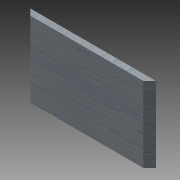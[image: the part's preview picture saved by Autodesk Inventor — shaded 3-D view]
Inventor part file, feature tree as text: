
AUTODESK INVENTOR PART (.ipt)
format: ipt  version: 2011 SP1 (Build 150282100, 282)  size: 86,528 bytes
history: native  units: in
note: dims shown in document units (in); Inventor stores cm internally (conversion verified against a paired STEP export)
features: extrude x1, chamfer x1, sketch x1
ambient origin geometry x8: Origin, YZ Plane, XZ Plane, XY Plane, X Axis, Y Axis, Z Axis, Center Point
bodies: Solid1 (feature_tree)
feature tree (3):
  extrude  "Extrusion1"  Depth=1.5in
  chamfer  "Chamfer1"  Distance=0.125in
  sketch  "Sketch1"  dims[d0=2.5in d1=1.5in d2=0.125in d3=0.0in d4=0.125in d5=0.125in d6=45.0deg]
